# Revit family: RVT_Macom_FVVx-xIT 03 23 A
name_source: partatom
category: Specialty Equipment
units: mm (PartAtom-declared; Revit-internal decimal feet)

## family parameters
Always vertical = Yes
Cut with Voids When Loaded = No
OmniClass Number = 23.40.40.11.11.11
OmniClass Title = Refrigerators
Part Type = Normal
Room Calculation Point = No
Round Connector Dimension = Use Diameter
Shared = No
Work Plane-Based = No

## types (2) — shared parameters
Default Elevation = 0,00 mm
Depth Actual = 800,00 mm
Door Width = 542,00 mm
Height Actual = 2060,00 mm
Manufacturer = MACOM
Show Clearances = Yes
Show Logo = Yes
URL = https://www.acosmacom.com.br
Volts = 220 V
Work Temperature = -21°C to -18°C

## per-type parameters (varying)
| type | Capacity | Description | Door 2 | Door QTY | Length Actual | Operational Current | Volume | Watts | Weight |
| FVVD-MIT | 800 L | FREEZER VERTICAL VERSATILE MAXI MACOM 2 PORTAS INOX, 20 TRILHOS, 10 CAIXAS PLASTICAS - 1140X800X2060 | Yes | 2 | 1140,00 mm | 5 A | 1,88 m³ | 774 W | 220,00 kg |
| FVVS-SIT | 410 L | FREEZER VERTICAL VERSATILE SLIM MACOM, 1 PORTA INOX, 10 TRILHOS, 5 CAIXAS PLASTICAS - 570X800X2060MM | No | 1 | 570,00 mm | 4 A | 0,94 m³ | 706 W | 150,00 kg |

note: column(s) folded — value = type name in every type: Model

## geometry (parser evidence)
native form markers: Sweep x3
no freeform markers — native parametric forms only
